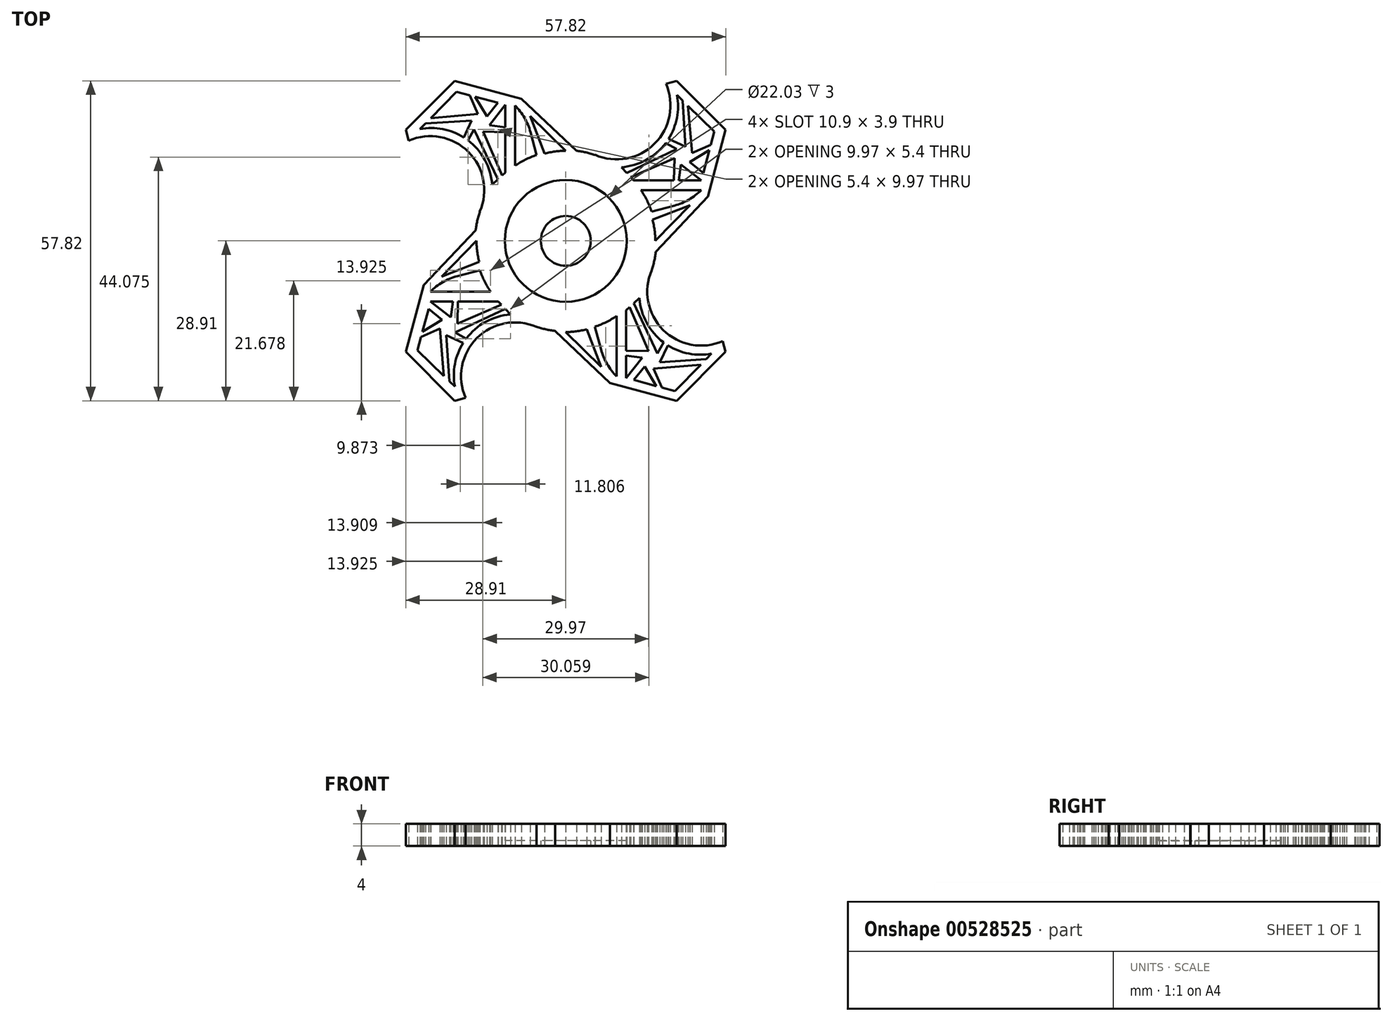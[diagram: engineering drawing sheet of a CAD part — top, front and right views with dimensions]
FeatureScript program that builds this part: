
annotation { "Feature Type Name" : "Feature", "Feature Type Description" : "" }
export const myFeature = defineFeature(function(context is Context, id is Id, definition is map)
    precondition{}
    {
        {
            var Q0;
            Q0=qCreatedBy(makeId("Top.planeOp"),FACE);
            var sketch = newSketch(context, id + "F0", { "sketchPlane" : qUnion([Q0])});
            skCircle(sketch, "E0", {"center": v(0, 0) * mm, "radius": 16.4 * mm});
            skSolve(sketch);
        }
        {
            var Q0;
            Q0=qSketchRegion(id+"F0",true);
            extrude(context, id + "F1", {"entities" : qUnion([Q0]), "depth" : 4 * mm, "offsetDistance" : 25 * mm});
        }
        {
            var Q0;
            Q0=qCreatedBy(makeId("Top.planeOp"),FACE);
            var sketch = newSketch(context, id + "F2", { "sketchPlane" : qUnion([Q0])});
            skLineSegment(sketch, "E1.bottom", {"start": v(-9.18, 9.18) * mm, "end": v(-24.49, 9.18) * mm});
            skLineSegment(sketch, "E1.top", {"start": v(-9.18, 24.49) * mm, "end": v(-24.49, 24.49) * mm});
            skLineSegment(sketch, "E1.left", {"start": v(-9.18, 9.18) * mm, "end": v(-9.18, 24.49) * mm});
            skLineSegment(sketch, "E1.right", {"start": v(-24.49, 9.18) * mm, "end": v(-24.49, 24.49) * mm});
            skPoint(sketch, "E2.oppositeSnap0", {"position": v(-16.84, 9.18) * mm});
            skLineSegment(sketch, "E3.bottom", {"start": v(-9.18, -9.18) * mm, "end": v(-24.49, -9.18) * mm});
            skLineSegment(sketch, "E3.top", {"start": v(-9.18, -24.49) * mm, "end": v(-24.49, -24.49) * mm});
            skLineSegment(sketch, "E3.left", {"start": v(-9.18, -9.18) * mm, "end": v(-9.18, -24.49) * mm});
            skLineSegment(sketch, "E3.right", {"start": v(-24.49, -9.18) * mm, "end": v(-24.49, -24.49) * mm});
            skLineSegment(sketch, "E4.bottom", {"start": v(9.18, -9.18) * mm, "end": v(24.49, -9.18) * mm});
            skLineSegment(sketch, "E4.top", {"start": v(9.18, -24.49) * mm, "end": v(24.49, -24.49) * mm});
            skLineSegment(sketch, "E4.left", {"start": v(9.18, -9.18) * mm, "end": v(9.18, -24.49) * mm});
            skLineSegment(sketch, "E4.right", {"start": v(24.49, -9.18) * mm, "end": v(24.49, -24.49) * mm});
            skLineSegment(sketch, "E5.bottom", {"start": v(9.18, 9.18) * mm, "end": v(24.49, 9.18) * mm});
            skLineSegment(sketch, "E5.top", {"start": v(9.18, 24.49) * mm, "end": v(24.49, 24.49) * mm});
            skLineSegment(sketch, "E5.left", {"start": v(9.18, 9.18) * mm, "end": v(9.18, 24.49) * mm});
            skLineSegment(sketch, "E5.right", {"start": v(24.49, 9.18) * mm, "end": v(24.49, 24.49) * mm});
            skCircle(sketch, "E6", {"center": v(16.84, -16.84) * mm, "radius": 10.82 * mm});
            skCircle(sketch, "E7", {"center": v(16.84, 16.84) * mm, "radius": 10.82 * mm});
            skCircle(sketch, "E8", {"center": v(-16.84, 16.84) * mm, "radius": 10.82 * mm});
            skCircle(sketch, "E9", {"center": v(-16.84, -16.84) * mm, "radius": 10.82 * mm});
            skCircle(sketch, "E10.cCircle", {"center": v(16.84, -16.84) * mm, "radius": 10.82 * mm, "construction": true});
            skLineSegment(sketch, "E10.0", {"start": v(28.9, -20.07) * mm, "end": v(20.07, -28.9) * mm});
            skLineSegment(sketch, "E10.1", {"start": v(20.07, -28.9) * mm, "end": v(8, -25.67) * mm});
            skLineSegment(sketch, "E10.2", {"start": v(8, -25.67) * mm, "end": v(4.76, -13.6) * mm});
            skLineSegment(sketch, "E10.3", {"start": v(4.76, -13.6) * mm, "end": v(13.6, -4.76) * mm});
            skLineSegment(sketch, "E10.4", {"start": v(13.6, -4.76) * mm, "end": v(25.67, -8) * mm});
            skLineSegment(sketch, "E10.5", {"start": v(25.67, -8) * mm, "end": v(28.9, -20.07) * mm});
            skPoint(sketch, "E10.0.midPoint", {"position": v(24.49, -24.49) * mm});
            skCircle(sketch, "E11.cCircle", {"center": v(-16.84, -16.84) * mm, "radius": 10.82 * mm, "construction": true});
            skLineSegment(sketch, "E11.0", {"start": v(-20.07, -28.9) * mm, "end": v(-28.9, -20.07) * mm});
            skLineSegment(sketch, "E11.1", {"start": v(-28.9, -20.07) * mm, "end": v(-25.67, -8) * mm});
            skLineSegment(sketch, "E11.2", {"start": v(-25.67, -8) * mm, "end": v(-13.6, -4.76) * mm});
            skLineSegment(sketch, "E11.3", {"start": v(-13.6, -4.76) * mm, "end": v(-4.76, -13.6) * mm});
            skLineSegment(sketch, "E11.4", {"start": v(-4.76, -13.6) * mm, "end": v(-8, -25.67) * mm});
            skLineSegment(sketch, "E11.5", {"start": v(-8, -25.67) * mm, "end": v(-20.07, -28.9) * mm});
            skPoint(sketch, "E11.0.midPoint", {"position": v(-24.49, -24.49) * mm});
            skCircle(sketch, "E12.cCircle", {"center": v(16.84, 16.84) * mm, "radius": 10.82 * mm, "construction": true});
            skLineSegment(sketch, "E12.0", {"start": v(20.07, 28.9) * mm, "end": v(28.9, 20.07) * mm});
            skLineSegment(sketch, "E12.1", {"start": v(28.9, 20.07) * mm, "end": v(25.67, 8) * mm});
            skLineSegment(sketch, "E12.2", {"start": v(25.67, 8) * mm, "end": v(13.6, 4.76) * mm});
            skLineSegment(sketch, "E12.3", {"start": v(13.6, 4.76) * mm, "end": v(4.76, 13.6) * mm});
            skLineSegment(sketch, "E12.4", {"start": v(4.76, 13.6) * mm, "end": v(8, 25.67) * mm});
            skLineSegment(sketch, "E12.5", {"start": v(8, 25.67) * mm, "end": v(20.07, 28.9) * mm});
            skPoint(sketch, "E12.0.midPoint", {"position": v(24.49, 24.49) * mm});
            skCircle(sketch, "E13.cCircle", {"center": v(-16.84, 16.84) * mm, "radius": 10.82 * mm, "construction": true});
            skLineSegment(sketch, "E13.0", {"start": v(-28.9, 20.07) * mm, "end": v(-20.07, 28.9) * mm});
            skLineSegment(sketch, "E13.1", {"start": v(-20.07, 28.9) * mm, "end": v(-8, 25.67) * mm});
            skLineSegment(sketch, "E13.2", {"start": v(-8, 25.67) * mm, "end": v(-4.76, 13.6) * mm});
            skLineSegment(sketch, "E13.3", {"start": v(-4.76, 13.6) * mm, "end": v(-13.6, 4.76) * mm});
            skLineSegment(sketch, "E13.4", {"start": v(-13.6, 4.76) * mm, "end": v(-25.67, 8) * mm});
            skLineSegment(sketch, "E13.5", {"start": v(-25.67, 8) * mm, "end": v(-28.9, 20.07) * mm});
            skPoint(sketch, "E13.0.midPoint", {"position": v(-24.49, 24.49) * mm});
            skLineSegment(sketch, "E14", {"start": v(-8, 25.67) * mm, "end": v(4.76, 13.6) * mm});
            skLineSegment(sketch, "E15", {"start": v(4.76, 13.6) * mm, "end": v(-4.76, 13.6) * mm});
            skLineSegment(sketch, "E16", {"start": v(25.67, 8) * mm, "end": v(13.6, -4.76) * mm});
            skLineSegment(sketch, "E17", {"start": v(13.6, 4.76) * mm, "end": v(13.6, -4.76) * mm});
            skLineSegment(sketch, "E18", {"start": v(-25.67, -8) * mm, "end": v(-13.6, 4.76) * mm});
            skLineSegment(sketch, "E19", {"start": v(-13.6, 4.76) * mm, "end": v(-13.6, -4.76) * mm});
            skLineSegment(sketch, "E20", {"start": v(8, -25.67) * mm, "end": v(-4.76, -13.6) * mm});
            skLineSegment(sketch, "E21", {"start": v(-4.76, -13.6) * mm, "end": v(4.76, -13.6) * mm});
            skSolve(sketch);
        }
        {
            var Q0;
            Q0=qSketchRegion(id+"F2",true);
            extrude(context, id + "F3", {"entities" : qUnion([Q0]), "operationType" : NewBodyOperationType.ADD, "depth" : 4 * mm, "offsetDistance" : 25 * mm});
        }
        {
            var Q0;
            Q0=sQuery(id+"F2.wireOp",VERTEX,"E1.right.start");
            var Q1;
            Q1=sQuery(id+"F2.wireOp",VERTEX,"E5.left.end");
            var Q2;
            Q2=sQuery(id+"F2.wireOp",VERTEX,"E4.right.start");
            var Q3;
            Q3=sQuery(id+"F2.wireOp",VERTEX,"E3.top.start");
            var Q4;
            Q4=makeQuery(id+"F1.opExtrude","SWEPT_BODY",BODY,{"disambiguationData":[OSD([sQuery(id+"F0.wireOp",EDGE,"E0")])]});
            hole(context, id + "F4", {"style" : HoleStyle.SIMPLE, "endStyle" : HoleEndStyle.THROUGH, "oppositeDirection" : true, "holeDiameter" : 19.5 * mm, "isTappedThrough" : true, "tappedDepth" : 12 * mm, "tapClearance" : 3, "locations" : qUnion([Q0, Q1, Q2, Q3]), "scope" : qUnion([Q4])});
        }
        {
            var Q0;
            Q0=qCreatedBy(makeId("Top.planeOp"),FACE);
            var sketch = newSketch(context, id + "F5", { "sketchPlane" : qUnion([Q0])});
            skLineSegment(sketch, "E22", {"start": v(10.93, -12.53) * mm, "end": v(10.93, -24.78) * mm});
            skLineSegment(sketch, "E23", {"start": v(19.76, -27.15) * mm, "end": v(26.35, -20.39) * mm});
            skArc(sketch, "E24", {"start": v(13.31, -10.36) * mm, "mid": v(17.59, -18.28) * mm, "end": v(26.35, -20.39) * mm});
            skLineSegment(sketch, "E25", {"start": v(13.31, -10.36) * mm, "end": v(10.93, -12.53) * mm});
            skLineSegment(sketch, "E26", {"start": v(12.29, -25.13) * mm, "end": v(19.76, -27.15) * mm});
            skLineSegment(sketch, "E27", {"start": v(10.93, -20.73) * mm, "end": v(13.82, -21.12) * mm});
            skLineSegment(sketch, "E28", {"start": v(17.03, -21.92) * mm, "end": v(25.37, -21.4) * mm});
            skLineSegment(sketch, "E29", {"start": v(18.44, -18.88) * mm, "end": v(17.03, -21.92) * mm});
            skLineSegment(sketch, "E30", {"start": v(10.93, -24.78) * mm, "end": v(13.82, -21.12) * mm});
            skLineSegment(sketch, "E31", {"start": v(16.57, -20.33) * mm, "end": v(12.29, -11.3) * mm});
            skLineSegment(sketch, "E32", {"start": v(14.27, -22.7) * mm, "end": v(16.4, -26.24) * mm});
            skLineSegment(sketch, "E33", {"start": v(15.88, -23.1) * mm, "end": v(17.38, -26.5) * mm});
            skLineSegment(sketch, "E34", {"start": v(12.29, -25.13) * mm, "end": v(14.27, -22.7) * mm});
            skLineSegment(sketch, "E35", {"start": v(16.57, -20.33) * mm, "end": v(17.68, -18.36) * mm});
            skLineSegment(sketch, "E36", {"start": v(15.88, -23.1) * mm, "end": v(24.4, -22.39) * mm});
            skLineSegment(sketch, "E37", {"start": v(10.93, -19.83) * mm, "end": v(14.97, -19.93) * mm});
            skLineSegment(sketch, "E38", {"start": v(14.97, -19.93) * mm, "end": v(11.51, -12) * mm});
            skLineSegment(sketch, "E39", {"start": v(6.43, -22.75) * mm, "end": v(0, -16.49) * mm});
            skLineSegment(sketch, "E40", {"start": v(6.43, -22.75) * mm, "end": v(3.8, -15.98) * mm});
            skArc(sketch, "E41", {"start": v(0, -16.49) * mm, "mid": v(1.92, -16.34) * mm, "end": v(3.8, -15.98) * mm});
            skLineSegment(sketch, "E42", {"start": v(12.25, 10.93) * mm, "end": v(24.5, 10.93) * mm});
            skLineSegment(sketch, "E43", {"start": v(26.87, 19.76) * mm, "end": v(20.1, 26.35) * mm});
            skArc(sketch, "E44", {"start": v(10.07, 13.31) * mm, "mid": v(18, 17.59) * mm, "end": v(20.1, 26.35) * mm});
            skLineSegment(sketch, "E45", {"start": v(10.07, 13.31) * mm, "end": v(12.25, 10.93) * mm});
            skLineSegment(sketch, "E46", {"start": v(24.85, 12.29) * mm, "end": v(26.87, 19.76) * mm});
            skLineSegment(sketch, "E47", {"start": v(20.44, 10.93) * mm, "end": v(20.83, 13.82) * mm});
            skLineSegment(sketch, "E48", {"start": v(21.63, 17.03) * mm, "end": v(21.1, 25.37) * mm});
            skLineSegment(sketch, "E49", {"start": v(18.59, 18.44) * mm, "end": v(21.63, 17.03) * mm});
            skLineSegment(sketch, "E50", {"start": v(24.5, 10.93) * mm, "end": v(20.83, 13.82) * mm});
            skLineSegment(sketch, "E51", {"start": v(20.04, 16.57) * mm, "end": v(11, 12.29) * mm});
            skLineSegment(sketch, "E52", {"start": v(22.42, 14.27) * mm, "end": v(25.96, 16.4) * mm});
            skLineSegment(sketch, "E53", {"start": v(22.82, 15.88) * mm, "end": v(26.22, 17.38) * mm});
            skLineSegment(sketch, "E54", {"start": v(24.85, 12.29) * mm, "end": v(22.42, 14.27) * mm});
            skLineSegment(sketch, "E55", {"start": v(20.04, 16.57) * mm, "end": v(18.07, 17.68) * mm});
            skLineSegment(sketch, "E56", {"start": v(22.82, 15.88) * mm, "end": v(22.1, 24.4) * mm});
            skLineSegment(sketch, "E57", {"start": v(19.54, 10.93) * mm, "end": v(19.64, 14.97) * mm});
            skLineSegment(sketch, "E58", {"start": v(19.64, 14.97) * mm, "end": v(11.72, 11.51) * mm});
            skLineSegment(sketch, "E59", {"start": v(22.46, 6.43) * mm, "end": v(16.2, 0) * mm});
            skLineSegment(sketch, "E60", {"start": v(22.46, 6.43) * mm, "end": v(15.7, 3.8) * mm});
            skArc(sketch, "E61", {"start": v(16.2, 0) * mm, "mid": v(16.06, 1.92) * mm, "end": v(15.7, 3.8) * mm});
            skLineSegment(sketch, "E62", {"start": v(-10.93, 12.35) * mm, "end": v(-10.93, 24.6) * mm});
            skLineSegment(sketch, "E63", {"start": v(-19.76, 26.98) * mm, "end": v(-26.35, 20.2) * mm});
            skArc(sketch, "E64", {"start": v(-13.31, 10.18) * mm, "mid": v(-17.59, 18.1) * mm, "end": v(-26.35, 20.2) * mm});
            skLineSegment(sketch, "E65", {"start": v(-13.31, 10.18) * mm, "end": v(-10.93, 12.35) * mm});
            skLineSegment(sketch, "E66", {"start": v(-12.29, 24.95) * mm, "end": v(-19.76, 26.98) * mm});
            skLineSegment(sketch, "E67", {"start": v(-10.93, 20.55) * mm, "end": v(-13.82, 20.94) * mm});
            skLineSegment(sketch, "E68", {"start": v(-17.03, 21.74) * mm, "end": v(-25.37, 21.22) * mm});
            skLineSegment(sketch, "E69", {"start": v(-18.44, 18.7) * mm, "end": v(-17.03, 21.74) * mm});
            skLineSegment(sketch, "E70", {"start": v(-10.93, 24.6) * mm, "end": v(-13.82, 20.94) * mm});
            skLineSegment(sketch, "E71", {"start": v(-16.57, 20.15) * mm, "end": v(-12.29, 11.11) * mm});
            skLineSegment(sketch, "E72", {"start": v(-14.27, 22.53) * mm, "end": v(-16.4, 26.06) * mm});
            skLineSegment(sketch, "E73", {"start": v(-15.88, 22.93) * mm, "end": v(-17.38, 26.33) * mm});
            skLineSegment(sketch, "E74", {"start": v(-12.29, 24.95) * mm, "end": v(-14.27, 22.53) * mm});
            skLineSegment(sketch, "E75", {"start": v(-16.57, 20.15) * mm, "end": v(-17.68, 18.18) * mm});
            skLineSegment(sketch, "E76", {"start": v(-15.88, 22.93) * mm, "end": v(-24.4, 22.2) * mm});
            skLineSegment(sketch, "E77", {"start": v(-10.93, 19.65) * mm, "end": v(-14.97, 19.75) * mm});
            skLineSegment(sketch, "E78", {"start": v(-14.97, 19.75) * mm, "end": v(-11.51, 11.82) * mm});
            skLineSegment(sketch, "E79", {"start": v(-6.43, 22.57) * mm, "end": v(0, 16.3) * mm});
            skLineSegment(sketch, "E80", {"start": v(-6.43, 22.57) * mm, "end": v(-3.8, 15.8) * mm});
            skArc(sketch, "E81", {"start": v(0, 16.3) * mm, "mid": v(-1.92, 16.16) * mm, "end": v(-3.8, 15.8) * mm});
            skLineSegment(sketch, "E82", {"start": v(-12.2, -10.93) * mm, "end": v(-24.43, -10.93) * mm});
            skLineSegment(sketch, "E83", {"start": v(-26.81, -19.76) * mm, "end": v(-20.04, -26.35) * mm});
            skArc(sketch, "E84", {"start": v(-10.02, -13.31) * mm, "mid": v(-17.94, -17.59) * mm, "end": v(-20.04, -26.35) * mm});
            skLineSegment(sketch, "E85", {"start": v(-10.02, -13.31) * mm, "end": v(-12.2, -10.93) * mm});
            skLineSegment(sketch, "E86", {"start": v(-24.8, -12.29) * mm, "end": v(-26.81, -19.76) * mm});
            skLineSegment(sketch, "E87", {"start": v(-20.38, -10.93) * mm, "end": v(-20.77, -13.82) * mm});
            skLineSegment(sketch, "E88", {"start": v(-21.58, -17.03) * mm, "end": v(-21.05, -25.37) * mm});
            skLineSegment(sketch, "E89", {"start": v(-18.53, -18.44) * mm, "end": v(-21.58, -17.03) * mm});
            skLineSegment(sketch, "E90", {"start": v(-24.43, -10.93) * mm, "end": v(-20.77, -13.82) * mm});
            skLineSegment(sketch, "E91", {"start": v(-19.99, -16.57) * mm, "end": v(-10.95, -12.29) * mm});
            skLineSegment(sketch, "E92", {"start": v(-22.37, -14.27) * mm, "end": v(-25.9, -16.4) * mm});
            skLineSegment(sketch, "E93", {"start": v(-22.77, -15.88) * mm, "end": v(-26.17, -17.38) * mm});
            skLineSegment(sketch, "E94", {"start": v(-24.8, -12.29) * mm, "end": v(-22.37, -14.27) * mm});
            skLineSegment(sketch, "E95", {"start": v(-19.99, -16.57) * mm, "end": v(-18.01, -17.68) * mm});
            skLineSegment(sketch, "E96", {"start": v(-22.77, -15.88) * mm, "end": v(-22.04, -24.4) * mm});
            skLineSegment(sketch, "E97", {"start": v(-19.49, -10.93) * mm, "end": v(-19.59, -14.97) * mm});
            skLineSegment(sketch, "E98", {"start": v(-19.59, -14.97) * mm, "end": v(-11.66, -11.51) * mm});
            skLineSegment(sketch, "E99", {"start": v(-22.4, -6.43) * mm, "end": v(-16.14, 0) * mm});
            skLineSegment(sketch, "E100", {"start": v(-22.4, -6.43) * mm, "end": v(-15.64, -3.8) * mm});
            skArc(sketch, "E101", {"start": v(-16.14, 0) * mm, "mid": v(-16, -1.92) * mm, "end": v(-15.64, -3.8) * mm});
            skSolve(sketch);
        }
        {
            var Q0;
            Q0=qSketchRegion(id+"F5",true);
            extrude(context, id + "F6", {"entities" : qUnion([Q0]), "operationType" : NewBodyOperationType.REMOVE, "endBound" : BoundingType.THROUGH_ALL, "depth" : 25 * mm, "offsetDistance" : 25 * mm});
        }
        {
            var Q0;
            Q0=makeQuery(id+"F1.opExtrude","SWEPT_BODY",BODY,{"disambiguationData":[OSD([sQuery(id+"F0.wireOp",EDGE,"E0")])]});
            var Q1;
            Q1=makeQuery(id+"FoOTqKo52XZLghF_1.hole-0.boolean.opBoolean","COPY",EDGE,{"derivedFrom":makeQuery(id+"FoOTqKo52XZLghF_1.hole-0.opRevolve","SWEPT_EDGE",EDGE,{"disambiguationData":[OSD([sQuery(id+"FoOTqKo52XZLghF_1.hole-0.sketch.wireOp",EDGE,"cbore_start_line_1"),sQuery(id+"FoOTqKo52XZLghF_1.hole-0.sketch.wireOp",EDGE,"core_line_2")])]})});
            transform(context, id + "F7", {"entities" : qUnion([Q0]), "transformType" : TransformType.TRANSLATION_3D, "dx" : 0 * mm, "dy" : 0 * mm, "dz" : 4 * mm, "makeCopy" : true});
        }
        {
            var Q0;
            Q0=makeQuery(id+"F7.opPattern","COPY",BODY,{"derivedFrom":makeQuery(id+"F1.opExtrude","SWEPT_BODY",BODY,{"disambiguationData":[OSD([sQuery(id+"F0.wireOp",EDGE,"E0")])]}),"instanceName":"1"});
            deleteBodies(context, id + "F8", {"entities" : qUnion([Q0])});
        }
        {
            var Q0;
            Q0=qCreatedBy(makeId("Top.planeOp"),FACE);
            var sketch = newSketch(context, id + "F9", { "sketchPlane" : qUnion([Q0])});
            skCircle(sketch, "E102", {"center": v(0, 0) * mm, "radius": 11.01 * mm});
            skSolve(sketch);
        }
        {
            var Q0;
            Q0 = qSketchRegion(id + "F9", true);
            extrude(context, id + "F10", {"entities" : qUnion([Q0]), "operationType" : NewBodyOperationType.REMOVE, "depth" : 4 * mm, "offsetDistance" : 25 * mm});
        }
        {
            var Q0;
            Q0=qCreatedBy(makeId("Top.planeOp"),FACE);
            var sketch = newSketch(context, id + "F11", { "sketchPlane" : qUnion([Q0])});
            skCircle(sketch, "E103", {"center": v(0, 0) * mm, "radius": 4.5 * mm});
            skSolve(sketch);
        }
        {
            var Q0;
            Q0 = qSketchRegion(id + "F9", true);
            extrude(context, id + "F12", {"entities" : qUnion([Q0]), "operationType" : NewBodyOperationType.ADD, "depth" : 1 * mm, "offsetDistance" : 25 * mm});
        }
        {
            var Q0;
            Q0 = qSketchRegion(id + "F11", true);
            extrude(context, id + "F13", {"entities" : qUnion([Q0]), "operationType" : NewBodyOperationType.REMOVE, "depth" : 1 * mm, "offsetDistance" : 25 * mm});
        }
    });
